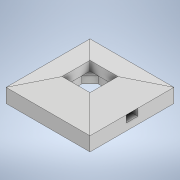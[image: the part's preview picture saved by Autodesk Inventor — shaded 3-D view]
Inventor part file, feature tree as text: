
AUTODESK INVENTOR PART (.ipt)
format: ipt  version: 2020 (Build 240168000, 168)  size: 190,464 bytes
history: native  units: mm
features: extrude x8, sketch x8
ambient origin geometry x8: Origin, YZ Plane, XZ Plane, XY Plane, X Axis, Y Axis, Z Axis, Center Point
bodies: Solid1 (feature_tree)
feature tree (16):
  extrude  "Extrusion1"  Depth=10.0mm
  extrude  "Extrusion2"  Depth=5.0mm
  extrude  "Extrusion3"  Depth=12.0mm
  extrude  "Extrusion4"  Depth=1.0mm
  extrude  "Extrusion5"  Depth=2.0mm TaperAngle=0.0deg
  extrude  "Extrusion6"  Depth=4.0mm
  extrude  "Extrusion7"  Depth=2.0mm
  extrude  "Extrusion8"  Depth=1.0mm TaperAngle=0.0deg
  sketch  "Sketch1"  dims[d0=10.0mm d1=10.0mm]
  sketch  "Sketch2"  dims[d2=5.0mm d3=5.0mm]
  sketch  "Sketch3"  dims[d4=12.0mm d5=12.0mm]
  sketch  "Sketch4"  dims[d6=1.0mm d7=1.0mm]
  sketch  "Sketch5"  dims[d8=2.0mm d9=0.0mm d10=11.5mm d11=0.0mm]
  sketch  "Sketch6"  dims[d13=4.0mm d14=4.0mm]
  sketch  "Sketch7"  dims[d15=2.0mm d16=2.0mm]
  sketch  "Sketch8"  dims[d17=23.25mm d18=0.0mm d19=1.0mm d20=0.0mm d21=25.0mm d22=0.0mm d23=4.0mm d24=23.25mm d25=0.0mm d26=41.75mm d27=0.0mm d28=11.625mm d29=0.0mm d30=4.0mm d31=4.0mm d32=105.0mm d33=0.0mm]
